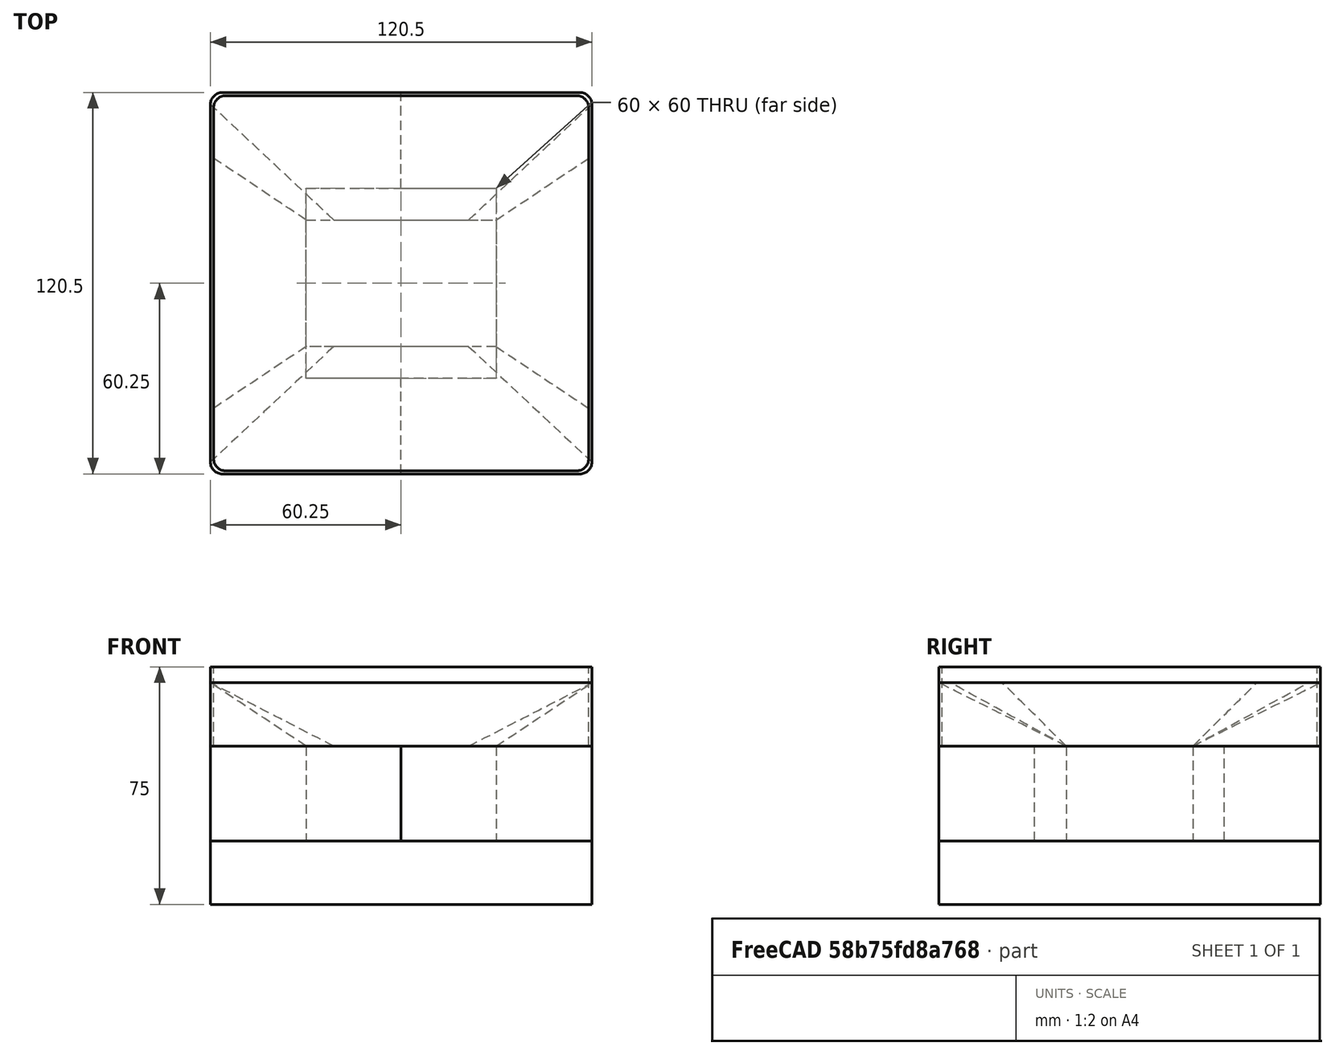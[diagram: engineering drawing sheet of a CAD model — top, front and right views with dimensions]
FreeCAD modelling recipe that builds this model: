
FCSTD DOCUMENT  (FreeCAD 0.20R29410 (Git))
Label: gridfinity_3x3_magnetshield
License: All rights reserved
LicenseURL: http://en.wikipedia.org/wiki/All_rights_reserved
objects: Sketcher::SketchObject×6, PartDesign::Pad×5, PartDesign::Body×5, Part::FeaturePython×3, Mesh::Feature×1, PartDesign::AdditiveLoft×1, PartDesign::Plane×1, App::DocumentObjectGroup×1
note: 27 computed .brp shape members not serialized (recipe doc carries the construction recipe); baked Part::Feature solids carry a one-line shape summary decoded from their .brp

FEATURE [Mesh::Feature] gridfinity_3x3x12_notag
FEATURE [Sketcher::SketchObject] Sketch
  FullyConstrained = true
  MapMode = 5
  Support = -> [XY_Plane]
  expr: Constraints[19] = 7.5 / 2
  expr: Constraints[21] = 41.5 * 3 - 4
  expr: Constraints[22] = (41.5 * 3 - 4) / 2
  expr: Constraints[23] = (41.5 * 3 - 4) / 2
  sketch-geometry (10):
    g0: ArcOfCircle CenterX=-56.5 CenterY=56.5 CenterZ=0 NormalX=0 NormalY=0 NormalZ=1 AngleXU=0 Radius=3.75 StartAngle=1.5708 EndAngle=3.14159
    g1: LineSegment StartX=-56.5 StartY=60.25 StartZ=0 EndX=56.5 EndY=60.25 EndZ=0
    g2: ArcOfCircle CenterX=56.5 CenterY=56.5 CenterZ=0 NormalX=0 NormalY=0 NormalZ=1 AngleXU=0 Radius=3.75 StartAngle=1.5e-15 EndAngle=1.5708
    g3: LineSegment StartX=60.25 StartY=56.5 StartZ=0 EndX=60.25 EndY=-56.5 EndZ=0
    g4: ArcOfCircle CenterX=56.5 CenterY=-56.5 CenterZ=0 NormalX=0 NormalY=0 NormalZ=1 AngleXU=0 Radius=3.75 StartAngle=4.71239 EndAngle=6.28319
    g5: LineSegment StartX=56.5 StartY=-60.25 StartZ=0 EndX=-56.5 EndY=-60.25 EndZ=0
    g6: ArcOfCircle CenterX=-56.5 CenterY=-56.5 CenterZ=0 NormalX=0 NormalY=0 NormalZ=1 AngleXU=0 Radius=3.75 StartAngle=3.14159 EndAngle=4.71239
    g7: LineSegment StartX=-60.25 StartY=-56.5 StartZ=0 EndX=-60.25 EndY=56.5 EndZ=0
    g8: GeomPoint X=-60.25 Y=60.25 Z=0
    g9: GeomPoint X=60.25 Y=-60.25 Z=0
  constraints (24):
    c: Tangent(g0,g1) = 1.5708
    c: Tangent(g1,g2) = 1.5708
    c: Tangent(g2,g3) = 1.5708
    c: Tangent(g3,g4) = 1.5708
    c: Tangent(g4,g5) = 1.5708
    c: Tangent(g5,g6) = 1.5708
    c: Tangent(g6,g7) = 1.5708
    c: Tangent(g7,g0) = 1.5708
    c: Horizontal(g1)
    c: Horizontal(g5)
    c: Vertical(g3)
    c: Vertical(g7)
    c: Equal(g0,g2)
    c: Equal(g2,g4)
    c: Equal(g4,g6)
    c: PointOnObject(g8,g1)
    c: PointOnObject(g8,g7)
    c: PointOnObject(g9,g3)
    c: PointOnObject(g9,g5)
    c: DistanceY(g0,g0) = 3.75
    c: Equal(g1,g3)
    c: DistanceX(g0,g2) = 120.5
    c: DistanceX(g8,g-1) = 60.25
    c: DistanceY(g9,g-1) = 60.25
FEATURE [PartDesign::Pad] Pad
  Direction = (0,0,1)
  Length = 20
  Length2 = 10
  Profile = -> Sketch
  ReferenceAxis = -> Sketch [N_Axis]
  Type = 0
FEATURE [PartDesign::Body] Body  label="base"
  Group = -> [Sketch,Pad]
  Origin = -> Origin
  Placement = pos=(0,0,7) rot=(0,0,1;0rad)
  Tip = -> Pad
FEATURE [Sketcher::SketchObject] Sketch001
  AttachmentOffset = pos=(0,0,15) rot=(0,0,1;0rad)
  FullyConstrained = true
  MapMode = 5
  Placement = pos=(0,0,15) rot=(0,0,1;0rad)
  Support = -> [XY_Plane001]
  sketch-geometry (4):
    g0: LineSegment StartX=-30 StartY=20 StartZ=0 EndX=30 EndY=20 EndZ=0
    g1: LineSegment StartX=30 StartY=20 StartZ=0 EndX=30 EndY=-20 EndZ=0
    g2: LineSegment StartX=30 StartY=-20 StartZ=0 EndX=-30 EndY=-20 EndZ=0
    g3: LineSegment StartX=-30 StartY=-20 StartZ=0 EndX=-30 EndY=20 EndZ=0
  constraints (12):
    c: Coincident(g0,g1)
    c: Coincident(g1,g2)
    c: Coincident(g2,g3)
    c: Coincident(g3,g0)
    c: Horizontal(g0)
    c: Horizontal(g2)
    c: Vertical(g1)
    c: Vertical(g3)
    c: DistanceX(g0,g0) = 60
    c: DistanceY(g1,g1) = 40
    c: DistanceX(g0,g-1) = 30
    c: DistanceY(g1,g-1) = 20
FEATURE [PartDesign::Pad] Pad001
  Direction = (0,0,1)
  Length = 30
  Length2 = 10
  Profile = -> Sketch001
  ReferenceAxis = -> Sketch001 [N_Axis]
  Reversed = true
  Type = 0
FEATURE [Sketcher::SketchObject] Sketch002
  AttachmentOffset = pos=(0,0,35) rot=(0,0,1;0rad)
  FullyConstrained = true
  MapMode = 5
  Placement = pos=(0,0,35) rot=(0,0,1;0rad)
  Support = -> [XY_Plane001]
  expr: Constraints[21] = 41.5 * 3 - 4
  expr: Constraints[22] = (41.5 * 3 - 4) / 2
  expr: Constraints[23] = (41.5 * 3 - 4) / 2
  sketch-geometry (10):
    g0: ArcOfCircle CenterX=-56.5 CenterY=56.5 CenterZ=0 NormalX=0 NormalY=0 NormalZ=1 AngleXU=0 Radius=3.75 StartAngle=1.5708 EndAngle=3.14159
    g1: LineSegment StartX=-56.5 StartY=60.25 StartZ=0 EndX=56.5 EndY=60.25 EndZ=0
    g2: ArcOfCircle CenterX=56.5 CenterY=56.5 CenterZ=0 NormalX=0 NormalY=0 NormalZ=1 AngleXU=0 Radius=3.75 StartAngle=-9e-16 EndAngle=1.5708
    g3: LineSegment StartX=60.25 StartY=56.5 StartZ=0 EndX=60.25 EndY=-56.5 EndZ=0
    g4: ArcOfCircle CenterX=56.5 CenterY=-56.5 CenterZ=0 NormalX=0 NormalY=0 NormalZ=1 AngleXU=0 Radius=3.75 StartAngle=4.71239 EndAngle=6.28319
    g5: LineSegment StartX=56.5 StartY=-60.25 StartZ=0 EndX=-56.5 EndY=-60.25 EndZ=0
    g6: ArcOfCircle CenterX=-56.5 CenterY=-56.5 CenterZ=0 NormalX=0 NormalY=0 NormalZ=1 AngleXU=0 Radius=3.75 StartAngle=3.14159 EndAngle=4.71239
    g7: LineSegment StartX=-60.25 StartY=-56.5 StartZ=0 EndX=-60.25 EndY=56.5 EndZ=0
    g8: GeomPoint X=-60.25 Y=60.25 Z=0
    g9: GeomPoint X=60.25 Y=-60.25 Z=0
  constraints (24):
    c: Tangent(g0,g1) = 1.5708
    c: Tangent(g1,g2) = 1.5708
    c: Tangent(g2,g3) = 1.5708
    c: Tangent(g3,g4) = 1.5708
    c: Tangent(g4,g5) = 1.5708
    c: Tangent(g5,g6) = 1.5708
    c: Tangent(g6,g7) = 1.5708
    c: Tangent(g7,g0) = 1.5708
    c: Horizontal(g1)
    c: Horizontal(g5)
    c: Vertical(g3)
    c: Vertical(g7)
    c: Equal(g0,g2)
    c: Equal(g2,g4)
    c: Equal(g4,g6)
    c: PointOnObject(g8,g1)
    c: PointOnObject(g8,g7)
    c: PointOnObject(g9,g3)
    c: PointOnObject(g9,g5)
    c: Equal(g1,g3)
    c: DistanceY(g0,g0) = 3.75
    c: DistanceX(g0,g2) = 120.5
    c: DistanceY(g5,g-1) = 60.25
    c: DistanceX(g6,g-1) = 60.25
FEATURE [PartDesign::AdditiveLoft] AdditiveLoft
  BaseFeature = -> Pad001
  Closed = false
  Profile = -> Sketch001
  Ruled = false
  Sections = -> [Sketch002]
FEATURE [PartDesign::Body] Body001  label="safe"
  Group = -> [Sketch001,Pad001,Sketch002,AdditiveLoft]
  Origin = -> Origin001
  Placement = pos=(0,0,42) rot=(0,0,1;0rad)
  Tip = -> AdditiveLoft
  expr: .Placement.Base.z = 7 + 35
FEATURE [Sketcher::SketchObject] Sketch003
  AttachmentOffset = pos=(0,0,27) rot=(0,0,1;0rad)
  FullyConstrained = true
  MapMode = 5
  Placement = pos=(0,0,27) rot=(0,0,1;0rad)
  Support = -> [XY_Plane002]
  expr: Constraints[21] = 41.5 * 3 - 4
  expr: Constraints[22] = (41.5 * 3 - 4) / 2
  expr: Constraints[23] = (41.5 * 3 - 4) / 2
  sketch-geometry (14):
    g0: ArcOfCircle CenterX=56.5 CenterY=56.5 CenterZ=0 NormalX=0 NormalY=0 NormalZ=1 AngleXU=0 Radius=3.75 StartAngle=-9e-16 EndAngle=1.5708
    g1: LineSegment StartX=60.25 StartY=56.5 StartZ=0 EndX=60.25 EndY=-56.5 EndZ=0
    g2: ArcOfCircle CenterX=56.5 CenterY=-56.5 CenterZ=0 NormalX=0 NormalY=0 NormalZ=1 AngleXU=0 Radius=3.75 StartAngle=4.71239 EndAngle=6.28319
    g3: LineSegment StartX=56.5 StartY=-60.25 StartZ=0 EndX=-56.5 EndY=-60.25 EndZ=0
    g4: ArcOfCircle CenterX=-56.5 CenterY=-56.5 CenterZ=0 NormalX=0 NormalY=0 NormalZ=1 AngleXU=0 Radius=3.75 StartAngle=3.14159 EndAngle=4.71239
    g5: LineSegment StartX=-60.25 StartY=-56.5 StartZ=0 EndX=-60.25 EndY=56.5 EndZ=0
    g6: ArcOfCircle CenterX=-56.5 CenterY=56.5 CenterZ=0 NormalX=0 NormalY=0 NormalZ=1 AngleXU=0 Radius=3.75 StartAngle=1.5708 EndAngle=3.14159
    g7: LineSegment StartX=-56.5 StartY=60.25 StartZ=0 EndX=56.5 EndY=60.25 EndZ=0
    g8: GeomPoint X=60.25 Y=60.25 Z=0
    g9: GeomPoint X=-60.25 Y=-60.25 Z=0
    g10: LineSegment StartX=-30 StartY=30 StartZ=0 EndX=30 EndY=30 EndZ=0
    g11: LineSegment StartX=30 StartY=30 StartZ=0 EndX=30 EndY=-30 EndZ=0
    g12: LineSegment StartX=30 StartY=-30 StartZ=0 EndX=-30 EndY=-30 EndZ=0
    g13: LineSegment StartX=-30 StartY=-30 StartZ=0 EndX=-30 EndY=30 EndZ=0
  constraints (36):
    c: Tangent(g0,g1) = 1.5708
    c: Tangent(g1,g2) = 1.5708
    c: Tangent(g2,g3) = 1.5708
    c: Tangent(g3,g4) = 1.5708
    c: Tangent(g4,g5) = 1.5708
    c: Tangent(g5,g6) = 1.5708
    c: Tangent(g6,g7) = 1.5708
    c: Tangent(g7,g0) = 1.5708
    c: Horizontal(g3)
    c: Horizontal(g7)
    c: Vertical(g1)
    c: Vertical(g5)
    c: Equal(g0,g2)
    c: Equal(g2,g4)
    c: Equal(g4,g6)
    c: PointOnObject(g8,g1)
    c: PointOnObject(g8,g7)
    c: PointOnObject(g9,g3)
    c: PointOnObject(g9,g5)
    c: Equal(g7,g5)
    c: DistanceY(g6,g6) = 3.75
    c: DistanceX(g5,g0) = 120.5
    c: DistanceY(g9,g-1) = 60.25
    c: DistanceX(g9,g-1) = 60.25
    c: Coincident(g10,g11)
    c: Coincident(g11,g12)
    c: Coincident(g12,g13)
    c: Coincident(g13,g10)
    c: Horizontal(g10)
    c: Horizontal(g12)
    c: Vertical(g11)
    c: Vertical(g13)
    c: DistanceX(g10,g10) = 60
    c: DistanceY(g11,g11) = 60
    c: DistanceX(g10,g-1) = 30
    c: DistanceY(g-1,g10) = 30
FEATURE [PartDesign::Pad] Pad002
  Direction = (0,0,1)
  Length = 30
  Length2 = 10
  Profile = -> Sketch003
  ReferenceAxis = -> Sketch003 [N_Axis]
  Type = 0
FEATURE [Sketcher::SketchObject] Sketch004
  AttachmentOffset = pos=(0,0,57) rot=(0,0,1;0rad)
  FullyConstrained = true
  MapMode = 5
  Placement = pos=(0,0,57) rot=(0,0,1;0rad)
  Support = -> [XY_Plane003]
  expr: Constraints[21] = 41.5 * 3 - 4
  expr: Constraints[22] = (41.5 * 3 - 4) / 2
  expr: Constraints[23] = (41.5 * 3 - 4) / 2
  sketch-geometry (10):
    g0: ArcOfCircle CenterX=-56.5 CenterY=56.5 CenterZ=0 NormalX=0 NormalY=0 NormalZ=1 AngleXU=0 Radius=3.75 StartAngle=1.5708 EndAngle=3.14159
    g1: LineSegment StartX=-56.5 StartY=60.25 StartZ=0 EndX=56.5 EndY=60.25 EndZ=0
    g2: ArcOfCircle CenterX=56.5 CenterY=56.5 CenterZ=0 NormalX=0 NormalY=0 NormalZ=1 AngleXU=0 Radius=3.75 StartAngle=0 EndAngle=1.5708
    g3: LineSegment StartX=60.25 StartY=56.5 StartZ=0 EndX=60.25 EndY=-56.5 EndZ=0
    g4: ArcOfCircle CenterX=56.5 CenterY=-56.5 CenterZ=0 NormalX=0 NormalY=0 NormalZ=1 AngleXU=0 Radius=3.75 StartAngle=4.71239 EndAngle=6.28319
    g5: LineSegment StartX=56.5 StartY=-60.25 StartZ=0 EndX=-56.5 EndY=-60.25 EndZ=0
    g6: ArcOfCircle CenterX=-56.5 CenterY=-56.5 CenterZ=0 NormalX=0 NormalY=0 NormalZ=1 AngleXU=0 Radius=3.75 StartAngle=3.14159 EndAngle=4.71239
    g7: LineSegment StartX=-60.25 StartY=-56.5 StartZ=0 EndX=-60.25 EndY=56.5 EndZ=0
    g8: GeomPoint X=-60.25 Y=60.25 Z=0
    g9: GeomPoint X=60.25 Y=-60.25 Z=0
  constraints (24):
    c: Tangent(g0,g1) = 1.5708
    c: Tangent(g1,g2) = 1.5708
    c: Tangent(g2,g3) = 1.5708
    c: Tangent(g3,g4) = 1.5708
    c: Tangent(g4,g5) = 1.5708
    c: Tangent(g5,g6) = 1.5708
    c: Tangent(g6,g7) = 1.5708
    c: Tangent(g7,g0) = 1.5708
    c: Horizontal(g1)
    c: Horizontal(g5)
    c: Vertical(g3)
    c: Vertical(g7)
    c: Equal(g0,g2)
    c: Equal(g2,g4)
    c: Equal(g4,g6)
    c: PointOnObject(g8,g1)
    c: PointOnObject(g8,g7)
    c: PointOnObject(g9,g3)
    c: PointOnObject(g9,g5)
    c: DistanceY(g0,g0) = 3.75
    c: Equal(g1,g3)
    c: DistanceX(g0,g2) = 120.5
    c: DistanceX(g6,g-1) = 60.25
    c: DistanceY(g9,g-1) = 60.25
FEATURE [PartDesign::Pad] Pad003
  Direction = (0,0,1)
  Length = 25
  Length2 = 10
  Profile = -> Sketch004
  ReferenceAxis = -> Sketch004 [N_Axis]
  Type = 0
FEATURE [PartDesign::Body] Body003  label="top"
  Group = -> [Sketch004,Pad003]
  Origin = -> Origin003
  Tip = -> Pad003
FEATURE [PartDesign::Plane] DatumPlane
  Length = 60
  MapMode = 4
  Placement = pos=(0,0,0) rot=(0.57735,0.57735,0.57735;2.0944rad)
  ResizeMode = 0
  Support = -> [Pad002]
  Width = 60
FEATURE [PartDesign::Body] Body002  label="shield"
  Group = -> [Sketch003,Pad002,DatumPlane]
  Origin = -> Origin002
  Tip = -> Pad002
FEATURE [Part::FeaturePython] Slice  # WARN: FeaturePython — macro-defined, semantics opaque (R4)
  Base = -> Pad002
  Mode = 1
  Tolerance = 0
  Tools = -> [DatumPlane]
FEATURE [Part::FeaturePython] Slice_child0  label="Slice.0"  # WARN: FeaturePython — macro-defined, semantics opaque (R4)
  Base = -> Slice
  FilterType = 1
  Invert = false
  OverrideMaxVal = 0
  WindowFrom = 80
  WindowTo = 100
  items = 0
FEATURE [Part::FeaturePython] Slice_child1  label="Slice.1"  # WARN: FeaturePython — macro-defined, semantics opaque (R4)
  Base = -> Slice
  FilterType = 1
  Invert = false
  OverrideMaxVal = 0
  WindowFrom = 80
  WindowTo = 100
  items = 1
FEATURE [App::DocumentObjectGroup] GrExplode_Slice  label="Exploded Slice"
  Group = -> [Slice_child0,Slice_child1]
FEATURE [Sketcher::SketchObject] Sketch005
  AttachmentOffset = pos=(0,0,57) rot=(0,0,1;0rad)
  FullyConstrained = true
  MapMode = 5
  Placement = pos=(0,0,57) rot=(0,0,1;0rad)
  Support = -> [XY_Plane004]
  expr: Constraints[21] = 41.5 * 3 - 6
  expr: Constraints[22] = (41.5 * 3 - 6) / 2
  expr: Constraints[23] = (41.5 * 3 - 6) / 2
  sketch-geometry (10):
    g0: ArcOfCircle CenterX=-55.5 CenterY=55.5 CenterZ=0 NormalX=0 NormalY=0 NormalZ=1 AngleXU=0 Radius=3.75 StartAngle=1.5708 EndAngle=3.14159
    g1: LineSegment StartX=-55.5 StartY=59.25 StartZ=0 EndX=55.5 EndY=59.25 EndZ=0
    g2: ArcOfCircle CenterX=55.5 CenterY=55.5 CenterZ=0 NormalX=0 NormalY=0 NormalZ=1 AngleXU=0 Radius=3.75 StartAngle=8e-16 EndAngle=1.5708
    g3: LineSegment StartX=59.25 StartY=55.5 StartZ=0 EndX=59.25 EndY=-55.5 EndZ=0
    g4: ArcOfCircle CenterX=55.5 CenterY=-55.5 CenterZ=0 NormalX=0 NormalY=0 NormalZ=1 AngleXU=0 Radius=3.75 StartAngle=4.71239 EndAngle=6.28319
    g5: LineSegment StartX=55.5 StartY=-59.25 StartZ=0 EndX=-55.5 EndY=-59.25 EndZ=0
    g6: ArcOfCircle CenterX=-55.5 CenterY=-55.5 CenterZ=0 NormalX=0 NormalY=0 NormalZ=1 AngleXU=0 Radius=3.75 StartAngle=3.14159 EndAngle=4.71239
    g7: LineSegment StartX=-59.25 StartY=-55.5 StartZ=0 EndX=-59.25 EndY=55.5 EndZ=0
    g8: GeomPoint X=-59.25 Y=59.25 Z=0
    g9: GeomPoint X=59.25 Y=-59.25 Z=0
  constraints (24):
    c: Tangent(g0,g1) = 1.5708
    c: Tangent(g1,g2) = 1.5708
    c: Tangent(g2,g3) = 1.5708
    c: Tangent(g3,g4) = 1.5708
    c: Tangent(g4,g5) = 1.5708
    c: Tangent(g5,g6) = 1.5708
    c: Tangent(g6,g7) = 1.5708
    c: Tangent(g7,g0) = 1.5708
    c: Horizontal(g1)
    c: Horizontal(g5)
    c: Vertical(g3)
    c: Vertical(g7)
    c: Equal(g0,g2)
    c: Equal(g2,g4)
    c: Equal(g4,g6)
    c: PointOnObject(g8,g1)
    c: PointOnObject(g8,g7)
    c: PointOnObject(g9,g3)
    c: PointOnObject(g9,g5)
    c: DistanceY(g0,g0) = 3.75
    c: Equal(g1,g3)
    c: DistanceX(g0,g2) = 118.5
    c: DistanceX(g6,g-1) = 59.25
    c: DistanceY(g9,g-1) = 59.25
FEATURE [PartDesign::Pad] Pad004
  Direction = (0,0,1)
  Length = 25
  Length2 = 10
  Profile = -> Sketch005
  ReferenceAxis = -> Sketch005 [N_Axis]
  Type = 0
FEATURE [PartDesign::Body] Body004  label="top001"
  Group = -> [Sketch005,Pad004]
  Origin = -> Origin004
  Tip = -> Pad004
